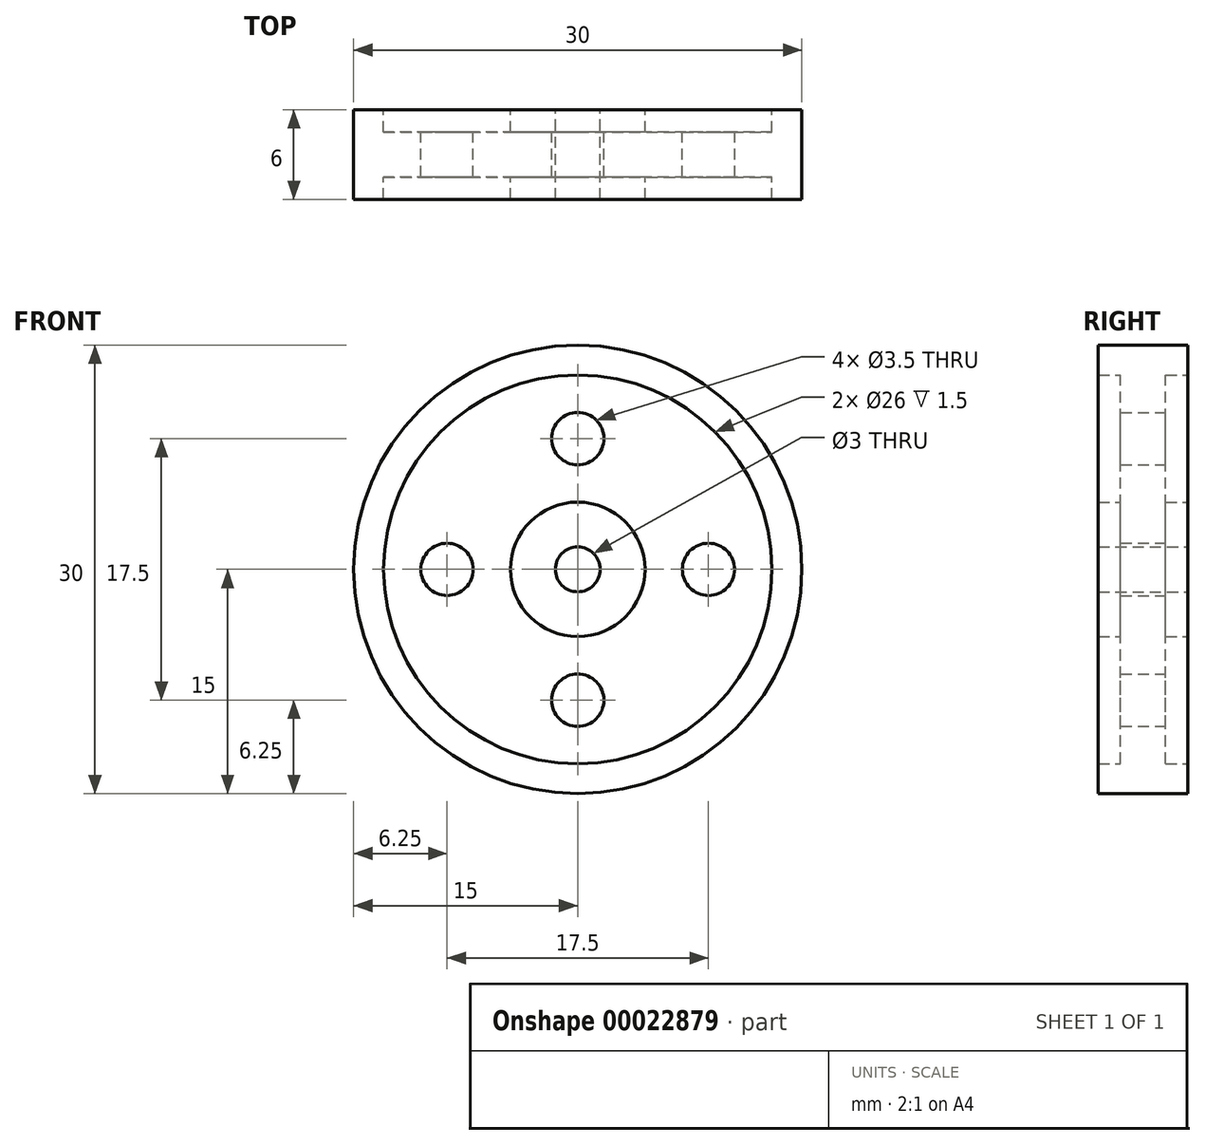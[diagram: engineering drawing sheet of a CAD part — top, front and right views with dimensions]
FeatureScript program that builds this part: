
annotation { "Feature Type Name" : "Feature", "Feature Type Description" : "" }
export const myFeature = defineFeature(function(context is Context, id is Id, definition is map)
    precondition{}
    {
        {
            var Q0;
            Q0=qCreatedBy(makeId("Front.planeOp"),FACE);
            var sketch = newSketch(context, id + "F0", { "sketchPlane" : qUnion([Q0])});
            skCircle(sketch, "E0", {"center": v(0, 0) * mm, "radius": 15 * mm});
            skCircle(sketch, "E1", {"center": v(0, 0) * mm, "radius": 4.5 * mm});
            skCircle(sketch, "E2", {"center": v(0, 0) * mm, "radius": 1.5 * mm});
            skCircle(sketch, "E3", {"center": v(0, 0) * mm, "radius": 13 * mm});
            skCircle(sketch, "E4", {"center": v(-8.75, 0) * mm, "radius": 1.75 * mm});
            skCircle(sketch, "E5.1.0", {"center": v(0, -8.75) * mm, "radius": 1.75 * mm});
            skCircle(sketch, "E5.2.0", {"center": v(8.75, 0) * mm, "radius": 1.75 * mm});
            skCircle(sketch, "E5.3.0", {"center": v(0, 8.75) * mm, "radius": 1.75 * mm});
            skSolve(sketch);
        }
        {
            var Q0;
            Q0=makeQuery(id+"F0.imprint","IMPRINT",FACE,{"disambiguationData":[TD([[makeQuery(id+"F0.imprint","IMPRINT",EDGE,{"derivedFrom":sQuery(id+"F0.wireOp",EDGE,"E0")}),1.0]])]});
            var Q1;
            Q1=makeQuery(id+"F0.imprint","IMPRINT",FACE,{"disambiguationData":[TD([[makeQuery(id+"F0.imprint","IMPRINT",EDGE,{"derivedFrom":sQuery(id+"F0.wireOp",EDGE,"E1")}),1.0]])]});
            extrude(context, id + "F1", {"entities" : qUnion([Q0, Q1]), "endBound" : BoundingType.SYMMETRIC, "depth" : 6 * mm});
        }
        {
            var Q0;
            Q0=makeQuery(id+"F0.imprint","IMPRINT",FACE,{"disambiguationData":[TD([[makeQuery(id+"F0.imprint","IMPRINT",EDGE,{"derivedFrom":sQuery(id+"F0.wireOp",EDGE,"E1")}),-1.0]])]});
            extrude(context, id + "F2", {"entities" : qUnion([Q0]), "operationType" : NewBodyOperationType.ADD, "endBound" : BoundingType.SYMMETRIC, "depth" : 3 * mm});
        }
    });
